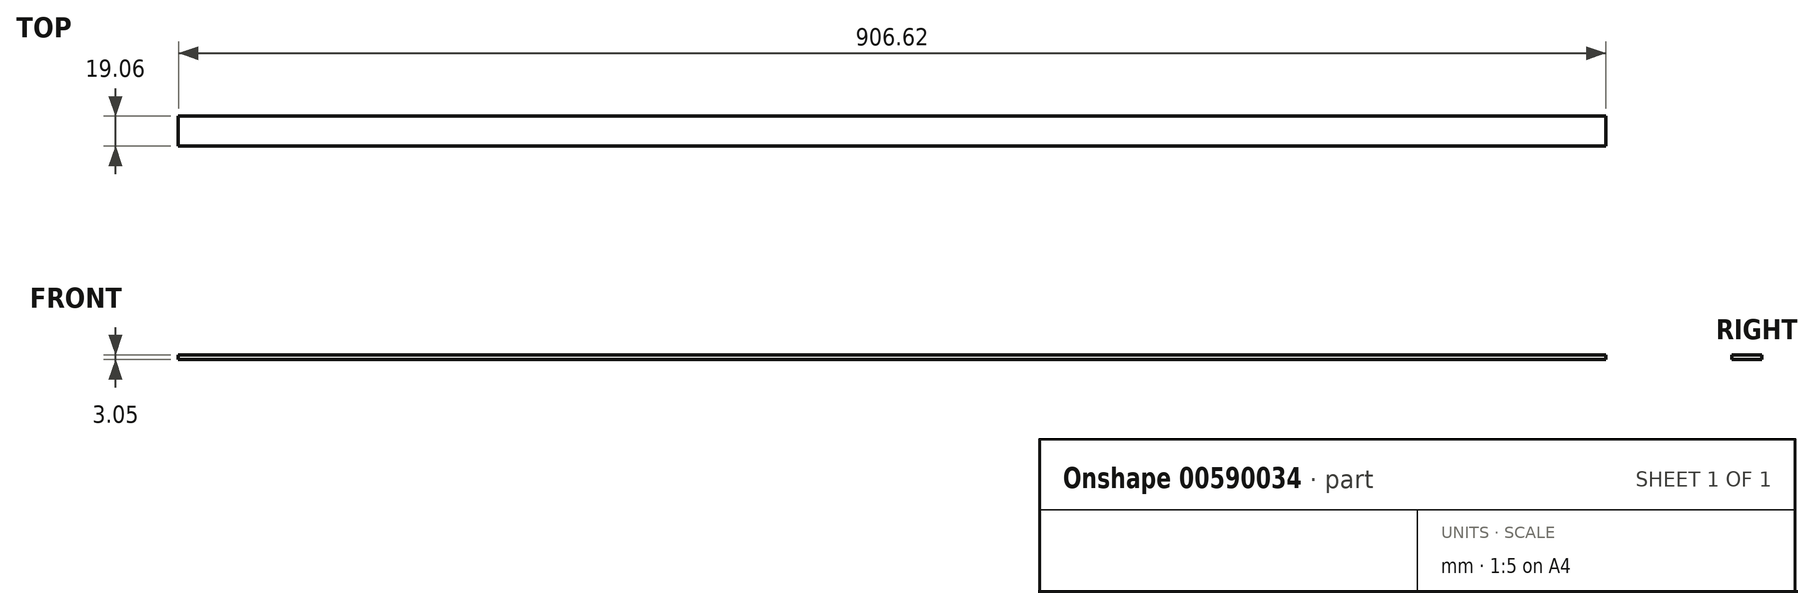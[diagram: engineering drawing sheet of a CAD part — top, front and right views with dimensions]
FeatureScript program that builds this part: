
annotation { "Feature Type Name" : "Feature", "Feature Type Description" : "" }
export const myFeature = defineFeature(function(context is Context, id is Id, definition is map)
    precondition{}
    {
        {
            var Q0;
            Q0=qCreatedBy(makeId("Right.planeOp"),FACE);
            var sketch = newSketch(context, id + "F0", { "sketchPlane" : qUnion([Q0])});
            skLineSegment(sketch, "E0.bottom", {"start": v(-9.52, 3.05) * mm, "end": v(9.52, 3.05) * mm});
            skLineSegment(sketch, "E0.top", {"start": v(-9.53, 0) * mm, "end": v(9.53, 0) * mm});
            skLineSegment(sketch, "E0.left", {"start": v(-9.53, 3.05) * mm, "end": v(-9.53, 0) * mm});
            skLineSegment(sketch, "E0.right", {"start": v(9.52, 3.05) * mm, "end": v(9.52, 0) * mm});
            skSolve(sketch);
        }
        {
            var Q0;
            Q0 = qSketchRegion(id + "F0", true);
            extrude(context, id + "F1", {"entities" : qUnion([Q0]), "endBound" : BoundingType.SYMMETRIC, "depth" : 906.63 * mm, "offsetDistance" : 25.4 * mm});
        }
    });
